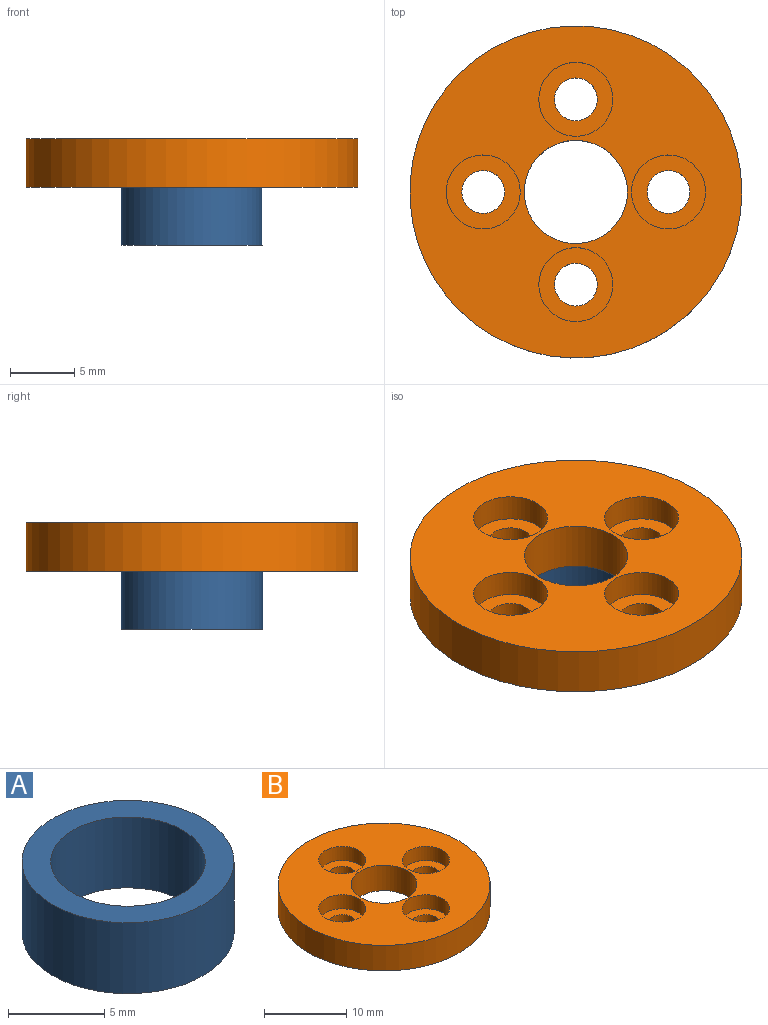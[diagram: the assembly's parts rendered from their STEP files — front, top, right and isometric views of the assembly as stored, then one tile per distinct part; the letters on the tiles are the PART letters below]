
ASSEMBLY  parts=2 mates=1
PART A: 4 faces, bbox 11x11x4.5 mm
  f0: cylinder r=4.01mm len=8.02mm, axis (0,0,1), area 113.3mm2, adj f2,f3
  f1: cylinder r=5.5mm len=11mm, axis (0,0,1), area 155.5mm2, adj f2,f3
  f2: plane 11x11mm, normal (0,0,-1), area 44.6mm2, adj f0,f1
  f3: plane 11x11mm, normal (0,0,1), area 44.6mm2, adj f0,f1
PART B: 16 faces, bbox 25.8x25.8x3.8 mm
  f0: cylinder r=1.66mm len=3.32mm, axis (0,0,1), area 17.7mm2, adj f6,f9
  f1: cylinder r=1.66mm len=3.32mm, axis (0,0,1), area 17.7mm2, adj f6,f13
  f2: cylinder r=1.66mm len=3.32mm, axis (0,0,1), area 17.7mm2, adj f6,f15
  f3: cylinder r=1.66mm len=3.32mm, axis (0,0,1), area 17.7mm2, adj f6,f11
  f4: cylinder r=12.9mm len=25.8mm, axis (0,0,1), area 308mm2, adj f6,f7
  f5: cylinder r=4.01mm len=8.02mm, axis (0,0,1), area 95.7mm2, adj f6,f7
  f6: plane 25.8x25.8mm, normal (0,0,-1), area 437.7mm2, adj f0,f1,f2,f3,f4,f5
  f7: plane 25.8x25.8mm, normal (0,0,1), area 368.5mm2, adj f4,f5,f8,f10,f12,f14
  f8: cylinder r=2.88mm len=5.75mm, axis (0,0,1), area 37.9mm2, adj f7,f9
  f9: plane 5.75x5.75mm, normal (0,0,1), area 17.3mm2, adj f0,f8
  f10: cylinder r=2.88mm len=5.75mm, axis (0,0,1), area 37.9mm2, adj f7,f11
  f11: plane 5.75x5.75mm, normal (0,0,1), area 17.3mm2, adj f3,f10
  f12: cylinder r=2.88mm len=5.75mm, axis (0,0,1), area 37.9mm2, adj f7,f13
  f13: plane 5.75x5.75mm, normal (0,0,1), area 17.3mm2, adj f1,f12
  f14: cylinder r=2.88mm len=5.75mm, axis (0,0,1), area 37.9mm2, adj f7,f15
  f15: plane 5.75x5.75mm, normal (0,0,1), area 17.3mm2, adj f2,f14
PLACE A t=(6.9,1.98,-4.37)mm
PLACE B t=(6.9,1.98,-4.37)mm
MATE fastened B.f5 <-> A.f0  axis (0,0,-1) through (6.9,1.98,-8.17)mm
